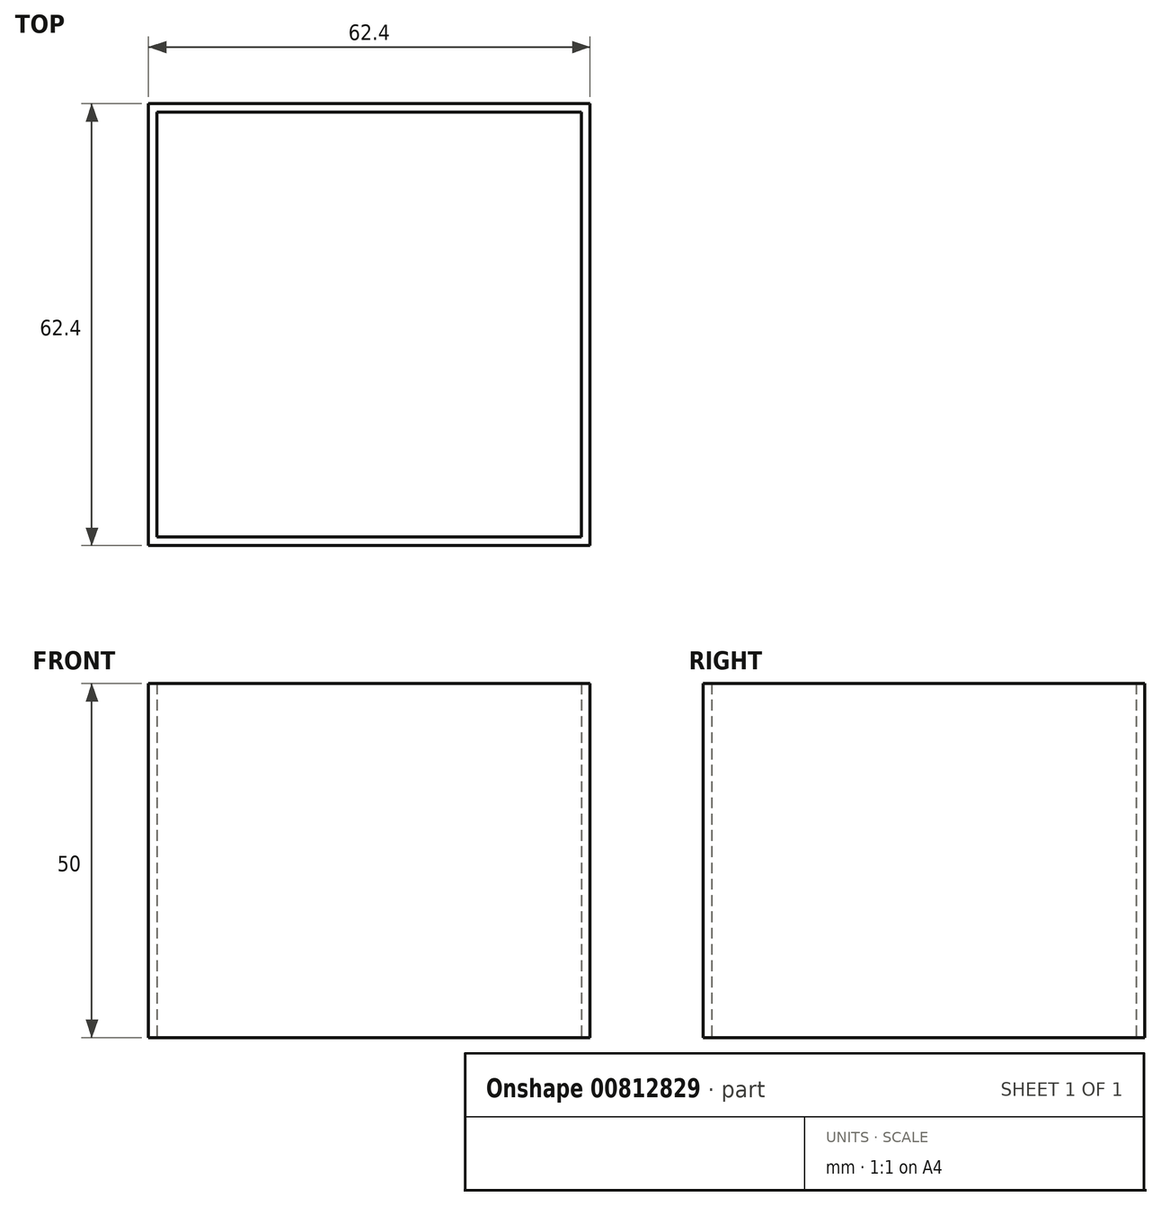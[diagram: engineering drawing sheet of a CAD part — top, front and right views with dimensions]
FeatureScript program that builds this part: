
annotation { "Feature Type Name" : "Feature", "Feature Type Description" : "" }
export const myFeature = defineFeature(function(context is Context, id is Id, definition is map)
    precondition{}
    {
        {
            var Q0;
            Q0=qCreatedBy(makeId("Top.planeOp"),FACE);
            var sketch = newSketch(context, id + "F0", { "sketchPlane" : qUnion([Q0])});
            skLineSegment(sketch, "E0.bottom", {"start": v(31.2, -31.2) * mm, "end": v(-31.2, -31.2) * mm});
            skLineSegment(sketch, "E0.left", {"start": v(31.2, -31.2) * mm, "end": v(31.2, 31.2) * mm});
            skLineSegment(sketch, "E0.right", {"start": v(-31.2, -31.2) * mm, "end": v(-31.2, 31.2) * mm});
            skPoint(sketch, "E0.middle", {"position": v(0, 0) * mm});
            skLineSegment(sketch, "E1", {"start": v(31.2, 31.2) * mm, "end": v(31.2, 31.2) * mm});
            skLineSegment(sketch, "E2", {"start": v(-31.2, 31.2) * mm, "end": v(31.2, 31.2) * mm});
            skLineSegment(sketch, "E3.bottom", {"start": v(30, -30) * mm, "end": v(-30, -30) * mm});
            skLineSegment(sketch, "E3.top", {"start": v(30, 30) * mm, "end": v(-30, 30) * mm});
            skLineSegment(sketch, "E3.left", {"start": v(30, -30) * mm, "end": v(30, 30) * mm});
            skLineSegment(sketch, "E3.right", {"start": v(-30, -30) * mm, "end": v(-30, 30) * mm});
            skSolve(sketch);
        }
        {
            var Q0;
            Q0 = qSketchRegion(id + "F0", true);
            var Q1;
            Q1=makeQuery(id+"F0.imprint","IMPRINT",FACE,{"disambiguationData":[TD([[makeQuery(id+"F0.imprint","IMPRINT",EDGE,{"derivedFrom":sQuery(id+"F0.wireOp",EDGE,"E0.bottom")}),-1.0]])]});
            extrude(context, id + "F1", {"entities" : qUnion([Q0, Q1]), "depth" : 50 * mm, "offsetDistance" : 25 * mm});
        }
    });
